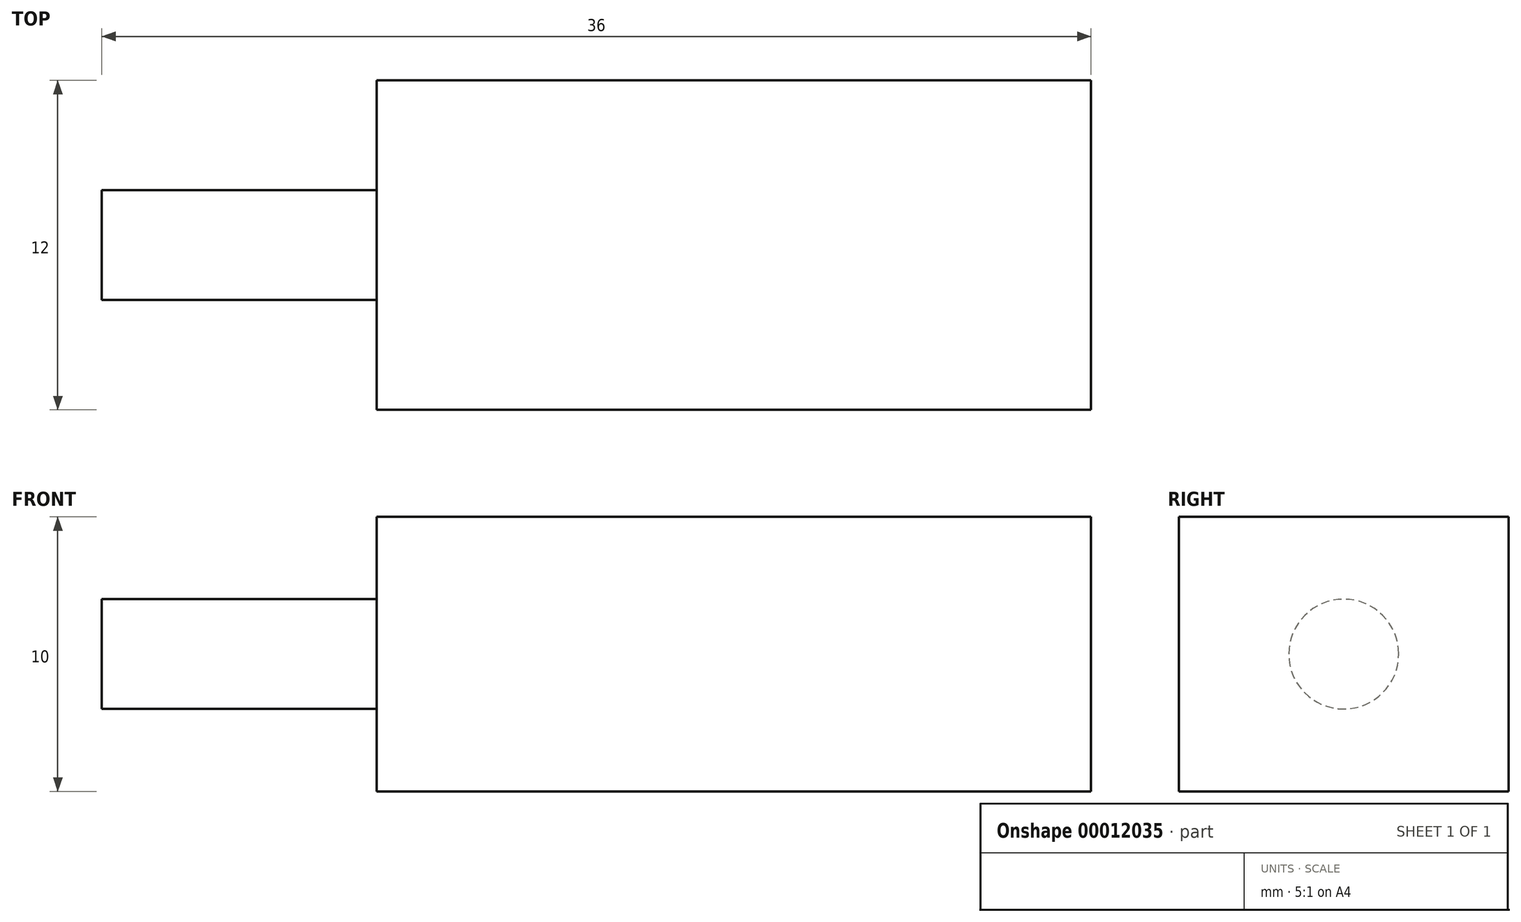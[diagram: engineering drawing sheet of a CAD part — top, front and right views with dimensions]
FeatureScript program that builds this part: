
annotation { "Feature Type Name" : "Feature", "Feature Type Description" : "" }
export const myFeature = defineFeature(function(context is Context, id is Id, definition is map)
    precondition{}
    {
        {
            var Q0;
            Q0=qCreatedBy(makeId("Right.planeOp"),FACE);
            var sketch = newSketch(context, id + "F0", { "sketchPlane" : qUnion([Q0])});
            skLineSegment(sketch, "E0.bottom", {"start": v(0, 0) * mm, "end": v(12, 0) * mm});
            skLineSegment(sketch, "E0.top", {"start": v(0, 10) * mm, "end": v(12, 10) * mm});
            skLineSegment(sketch, "E0.left", {"start": v(0, 0) * mm, "end": v(0, 10) * mm});
            skLineSegment(sketch, "E0.right", {"start": v(12, 0) * mm, "end": v(12, 10) * mm});
            skSolve(sketch);
        }
        {
            var Q0;
            Q0=makeQuery(id+"F0.imprint","IMPRINT",FACE,{"disambiguationData":[TD([[makeQuery(id+"F0.imprint","IMPRINT",EDGE,{"derivedFrom":sQuery(id+"F0.wireOp",EDGE,"E0.bottom")}),1.0]])]});
            extrude(context, id + "F1", {"entities" : qUnion([Q0]), "depth" : 26 * mm});
        }
        {
            var Q0;
            Q0=makeQuery(id+"F1.opExtrude","CAP_FACE",FACE,{"disambiguationData":[OSD([sQuery(id+"F0.wireOp",EDGE,"E0.bottom"),sQuery(id+"F0.wireOp",EDGE,"E0.top"),sQuery(id+"F0.wireOp",EDGE,"E0.left"),sQuery(id+"F0.wireOp",EDGE,"E0.right")])],"isStart":true});
            var sketch = newSketch(context, id + "F2", { "sketchPlane" : qUnion([Q0])});
            skCircle(sketch, "E1", {"center": v(-6, 5) * mm, "radius": 2 * mm});
            skLineSegment(sketch, "E2", {"start": v(-6, 10) * mm, "end": v(-6, 0) * mm, "construction": true});
            skSolve(sketch);
        }
        {
            var Q0;
            Q0=makeQuery(id+"F2.imprint","IMPRINT",FACE,{"disambiguationData":[TD([[makeQuery(id+"F2.imprint","IMPRINT",EDGE,{"derivedFrom":sQuery(id+"F2.wireOp",EDGE,"E1")}),1.0]])]});
            extrude(context, id + "F3", {"entities" : qUnion([Q0]), "operationType" : NewBodyOperationType.ADD, "depth" : 10 * mm});
        }
    });
